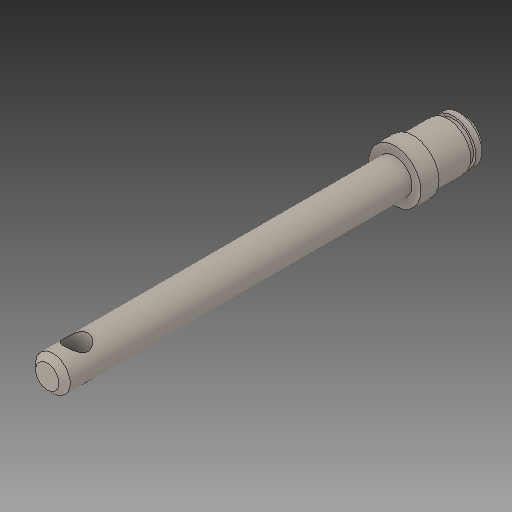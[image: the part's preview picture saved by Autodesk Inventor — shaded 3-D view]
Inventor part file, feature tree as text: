
AUTODESK INVENTOR PART (.ipt)
format: ipt  version: 2018 (Build 220112000, 112)  size: 114,176 bytes
history: native  units: in
note: dims shown in document units (in); Inventor stores cm internally (conversion verified against a paired STEP export)
features: chamfer x1
ambient origin geometry x8: Origin, YZ Plane, XZ Plane, XY Plane, X Axis, Y Axis, Z Axis, Center Point
bodies: Solid1 (feature_tree)
feature tree (1):
  chamfer  "Chamfer1"  [1 undecoded]
note: 1 required parameter value undecoded (feature->parameter linkage not recoverable at this tier; creation-order binding heuristic only, values carry confidence <= 0.55)
